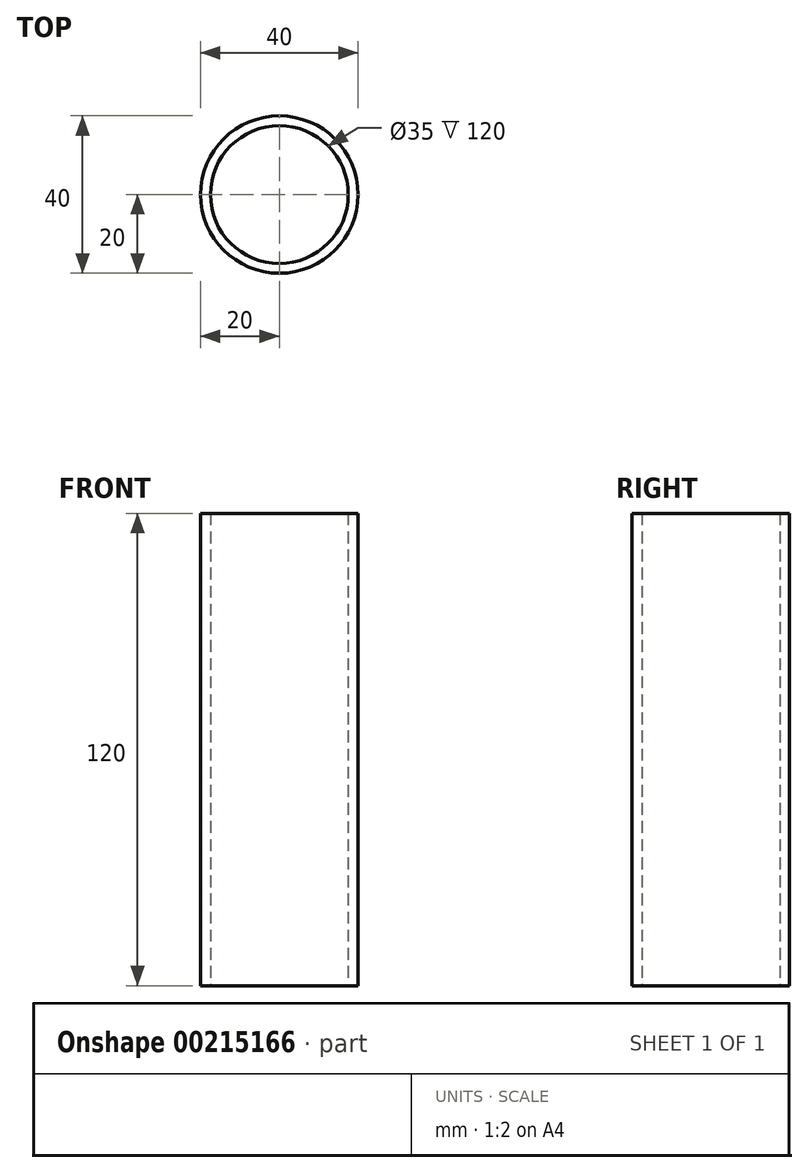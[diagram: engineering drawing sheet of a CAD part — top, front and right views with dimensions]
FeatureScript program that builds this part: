
annotation { "Feature Type Name" : "Feature", "Feature Type Description" : "" }
export const myFeature = defineFeature(function(context is Context, id is Id, definition is map)
    precondition{}
    {
        {
            var Q0;
            Q0=qCreatedBy(makeId("Top.planeOp"),FACE);
            var sketch = newSketch(context, id + "F0", { "sketchPlane" : qUnion([Q0])});
            skCircle(sketch, "E0", {"center": v(0, 0) * mm, "radius": 20 * mm});
            skCircle(sketch, "E1", {"center": v(0, 0) * mm, "radius": 17.5 * mm});
            skSolve(sketch);
        }
        {
            var Q0;
            Q0 = qSketchRegion(id + "F0", true);
            extrude(context, id + "F1", {"entities" : qUnion([Q0]), "depth" : 120 * mm});
        }
    });
